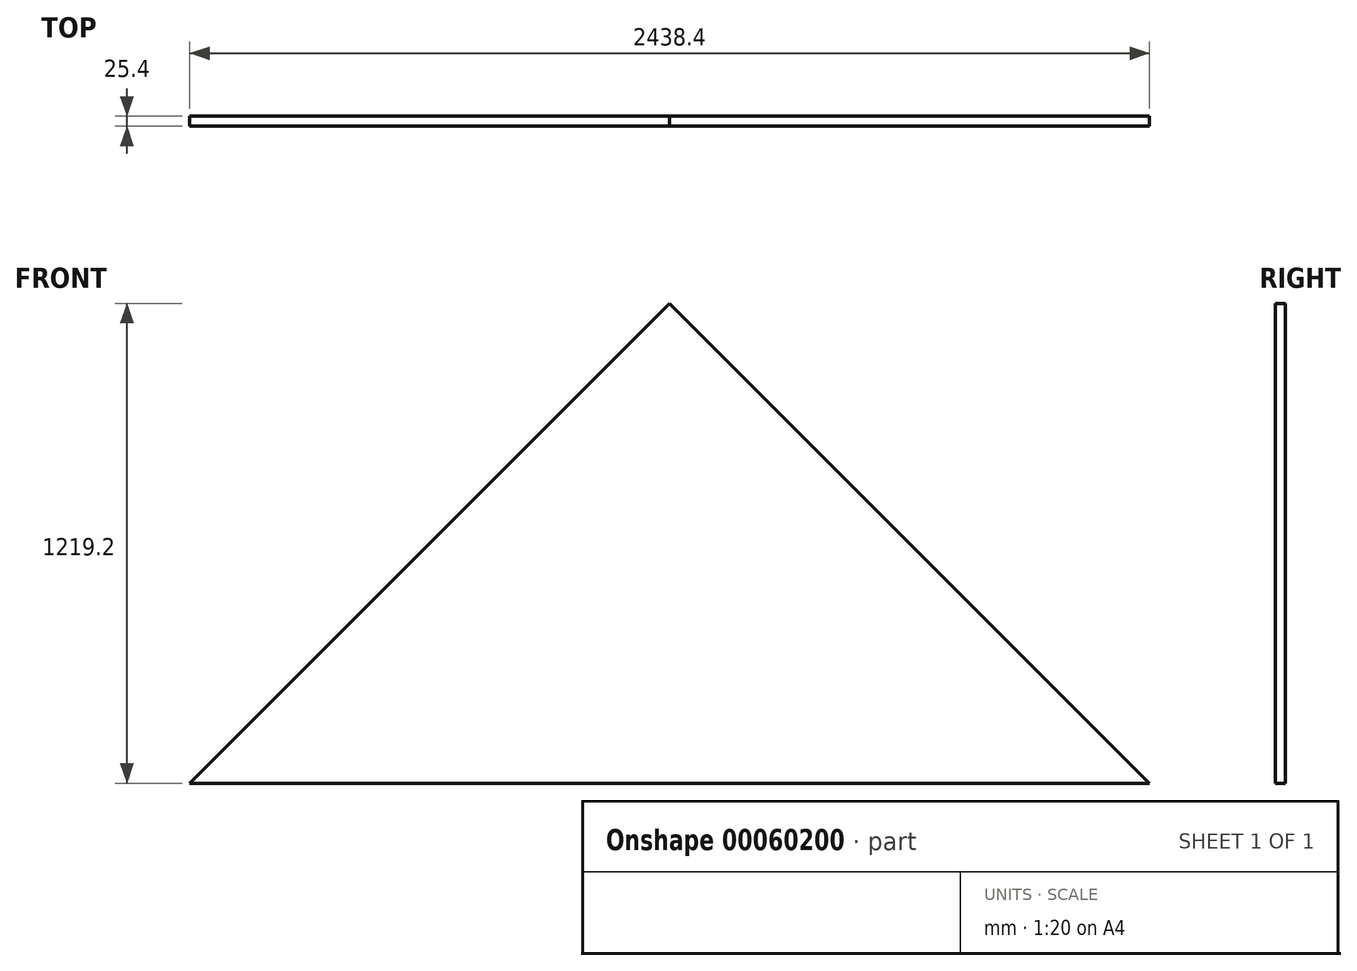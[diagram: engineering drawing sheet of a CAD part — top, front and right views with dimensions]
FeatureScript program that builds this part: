
annotation { "Feature Type Name" : "Feature", "Feature Type Description" : "" }
export const myFeature = defineFeature(function(context is Context, id is Id, definition is map)
    precondition{}
    {
        {
            var Q0;
            Q0=qCreatedBy(makeId("Front.planeOp"),FACE);
            var sketch = newSketch(context, id + "F1", { "sketchPlane" : qUnion([Q0])});
            skLineSegment(sketch, "E0", {"start": v(-1219.2, -291.97) * mm, "end": v(0, 927.23) * mm});
            skLineSegment(sketch, "E1", {"start": v(0, 927.23) * mm, "end": v(1219.2, -291.97) * mm});
            skLineSegment(sketch, "E2", {"start": v(-1219.2, -291.97) * mm, "end": v(1219.2, -291.97) * mm});
            skSolve(sketch);
        }
        {
            var Q0;
            Q0=makeQuery(id+"F1.imprint","IMPRINT",FACE,{"disambiguationData":[TD([[makeQuery(id+"F1.imprint","IMPRINT",EDGE,{"derivedFrom":sQuery(id+"F1.wireOp",EDGE,"E0")}),-1.0]])]});
            extrude(context, id + "F0", {"entities" : qUnion([Q0]), "depth" : 25.4 * mm});
        }
    });
